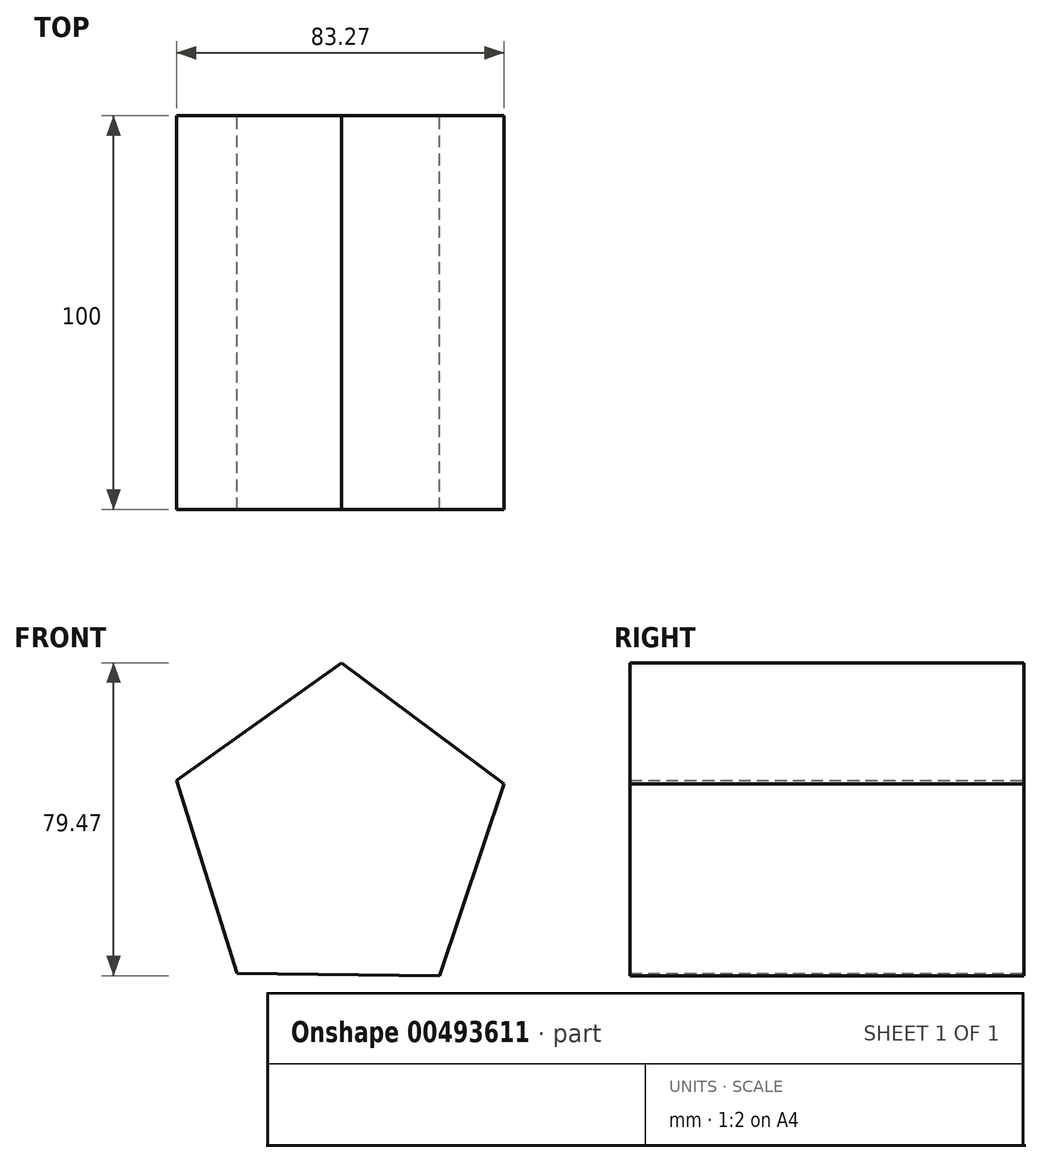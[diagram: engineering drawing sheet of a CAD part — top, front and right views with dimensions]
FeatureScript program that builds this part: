
annotation { "Feature Type Name" : "Feature", "Feature Type Description" : "" }
export const myFeature = defineFeature(function(context is Context, id is Id, definition is map)
    precondition{}
    {
        {
            var Q0;
            Q0=qCreatedBy(makeId("Front.planeOp"),FACE);
            var sketch = newSketch(context, id + "F0", { "sketchPlane" : qUnion([Q0])});
            skCircle(sketch, "E0.cCircle", {"center": v(0, 0) * mm, "radius": 43.78 * mm, "construction": true});
            skLineSegment(sketch, "E0.0", {"start": v(-26.1, -35.14) * mm, "end": v(-41.5, 13.97) * mm});
            skLineSegment(sketch, "E0.1", {"start": v(-41.5, 13.97) * mm, "end": v(0.46, 43.78) * mm});
            skLineSegment(sketch, "E0.2", {"start": v(0.46, 43.78) * mm, "end": v(41.78, 13.09) * mm});
            skLineSegment(sketch, "E0.3", {"start": v(41.78, 13.09) * mm, "end": v(25.36, -35.69) * mm});
            skLineSegment(sketch, "E0.4", {"start": v(25.36, -35.69) * mm, "end": v(-26.1, -35.14) * mm});
            skSolve(sketch);
        }
        {
            var Q0;
            Q0=makeQuery(id+"F0.imprint","IMPRINT",FACE,{"disambiguationData":[TD([[makeQuery(id+"F0.imprint","IMPRINT",EDGE,{"derivedFrom":sQuery(id+"F0.wireOp",EDGE,"E0.0")}),-1.0]])]});
            extrude(context, id + "F1", {"entities" : qUnion([Q0]), "depth" : 100 * mm});
        }
    });
